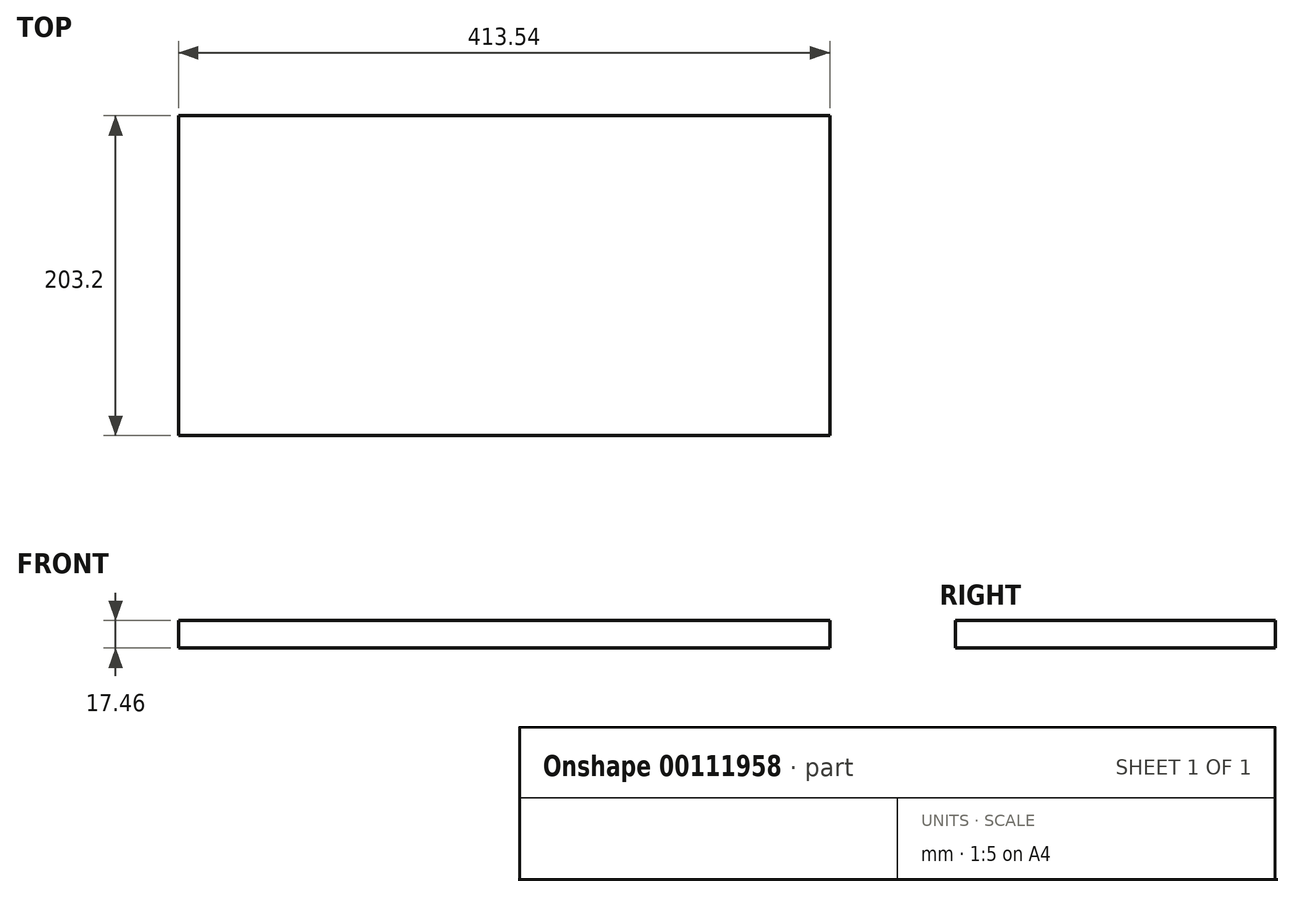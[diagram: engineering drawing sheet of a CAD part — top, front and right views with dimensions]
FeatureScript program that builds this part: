
annotation { "Feature Type Name" : "Feature", "Feature Type Description" : "" }
export const myFeature = defineFeature(function(context is Context, id is Id, definition is map)
    precondition{}
    {
        {
            var Q0;
            Q0=qCreatedBy(makeId("Top.planeOp"),FACE);
            var sketch = newSketch(context, id + "F0", { "sketchPlane" : qUnion([Q0])});
            skLineSegment(sketch, "E0.bottom", {"start": v(-206.77, 101.6) * mm, "end": v(206.77, 101.6) * mm});
            skLineSegment(sketch, "E0.top", {"start": v(-206.77, -101.6) * mm, "end": v(206.77, -101.6) * mm});
            skLineSegment(sketch, "E0.left", {"start": v(-206.77, 101.6) * mm, "end": v(-206.77, -101.6) * mm});
            skLineSegment(sketch, "E0.right", {"start": v(206.77, 101.6) * mm, "end": v(206.77, -101.6) * mm});
            skPoint(sketch, "E0.middle", {"position": v(0, 0) * mm});
            skSolve(sketch);
        }
        {
            var Q0;
            Q0=makeQuery(id+"F0.imprint","IMPRINT",FACE,{"disambiguationData":[TD([[makeQuery(id+"F0.imprint","IMPRINT",EDGE,{"derivedFrom":sQuery(id+"F0.wireOp",EDGE,"E0.bottom")}),-1.0]])]});
            extrude(context, id + "F1", {"entities" : qUnion([Q0]), "depth" : 17.46 * mm});
        }
    });
